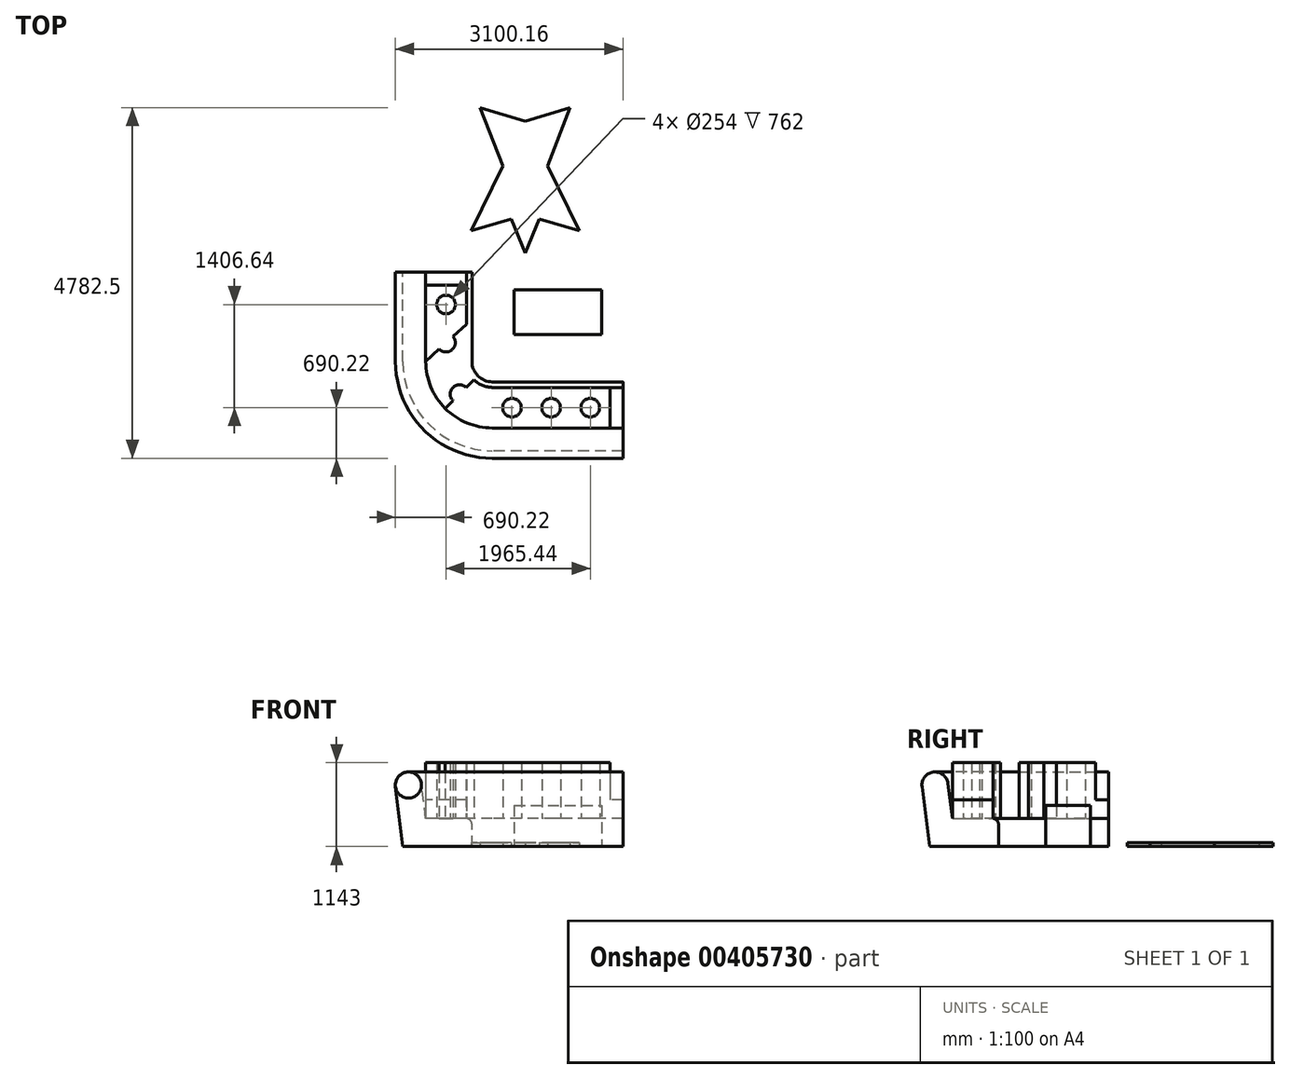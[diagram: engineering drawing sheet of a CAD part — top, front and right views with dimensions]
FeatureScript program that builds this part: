
annotation { "Feature Type Name" : "Feature", "Feature Type Description" : "" }
export const myFeature = defineFeature(function(context is Context, id is Id, definition is map)
    precondition{}
    {
        {
            var Q0;
            Q0=qCreatedBy(makeId("Right.planeOp"),FACE);
            var sketch = newSketch(context, id + "F0", { "sketchPlane" : qUnion([Q0])});
            skLineSegment(sketch, "E0", {"start": v(-101.6, 816.24) * mm, "end": v(0, 0) * mm});
            skLineSegment(sketch, "E1", {"start": v(0, 0) * mm, "end": v(939.8, 0) * mm});
            skLineSegment(sketch, "E2", {"start": v(939.8, 0) * mm, "end": v(939.8, 304.8) * mm});
            skLineSegment(sketch, "E3", {"start": v(863.6, 381) * mm, "end": v(310.92, 381) * mm});
            skLineSegment(sketch, "E4", {"start": v(310.92, 381) * mm, "end": v(251.28, 860.16) * mm});
            skLineSegment(sketch, "E5", {"start": v(251.28, 860.16) * mm, "end": v(-101.6, 816.24) * mm});
            skArc(sketch, "E6", {"start": v(251.28, 860.16) * mm, "mid": v(52.88, 1014.64) * mm, "end": v(-101.6, 816.24) * mm});
            skPoint(sketch, "E7.visualSharp", {"position": v(939.8, 381) * mm});
            skArc(sketch, "E7.filletArc", {"start": v(939.8, 304.8) * mm, "mid": v(917.48, 358.68) * mm, "end": v(863.6, 381) * mm});
            skSolve(sketch);
        }
        {
            var Q0;
            Q0=qCreatedBy(makeId("Top.planeOp"),FACE);
            var sketch = newSketch(context, id + "F1", { "sketchPlane" : qUnion([Q0])});
            skLineSegment(sketch, "E8", {"start": v(0, 0) * mm, "end": v(-1778, 0) * mm});
            skLineSegment(sketch, "E9", {"start": v(-2997.2, 1219.2) * mm, "end": v(-2997.2, 2438.4) * mm});
            skArc(sketch, "E10", {"start": v(-2997.2, 1219.2) * mm, "mid": v(-2640.1, 357.1) * mm, "end": v(-1778, 0) * mm});
            skSolve(sketch);
        }
        {
            var Q0;
            Q0=makeQuery(id+"F0.imprint","IMPRINT",FACE,{"disambiguationData":[TD([[makeQuery(id+"F0.imprint","IMPRINT",EDGE,{"derivedFrom":sQuery(id+"F0.wireOp",EDGE,"E0")}),1.0]])]});
            var Q1;
            Q1=makeQuery(id+"F0.imprint","IMPRINT",FACE,{"disambiguationData":[TD([[makeQuery(id+"F0.imprint","IMPRINT",EDGE,{"derivedFrom":sQuery(id+"F0.wireOp",EDGE,"E5")}),-1.0]])]});
            var Q2;
            Q2=sQuery(id+"F1.wireOp",EDGE,"E8");
            var Q3;
            Q3=sQuery(id+"F1.wireOp",EDGE,"E10");
            var Q4;
            Q4=sQuery(id+"F1.wireOp",EDGE,"E9");
            sweep(context, id + "F2", {"profiles" : qUnion([Q0, Q1]), "path" : qUnion([Q2, Q3, Q4])});
        }
        {
            var Q0;
            Q0=makeQuery(id+"F2.opSweep","SWEPT_FACE",FACE,{"disambiguationData":[OSD([sQuery(id+"F0.wireOp",EDGE,"E3"),sQuery(id+"F1.wireOp",EDGE,"E8")])]});
            var sketch = newSketch(context, id + "F3", { "sketchPlane" : qUnion([Q0])});
            skLineSegment(sketch, "E11.0", {"start": v(0, 863.6) * mm, "end": v(-1778, 863.6) * mm});
            skArc(sketch, "E11.1", {"start": v(-1778, 863.6) * mm, "mid": v(-2029.45, 967.75) * mm, "end": v(-2133.6, 1219.2) * mm});
            skLineSegment(sketch, "E11.2", {"start": v(-2133.6, 1219.2) * mm, "end": v(-2133.6, 2438.4) * mm});
            skLineSegment(sketch, "E11.3", {"start": v(-2686.28, 2438.4) * mm, "end": v(-2133.6, 2438.4) * mm});
            skLineSegment(sketch, "E11.4", {"start": v(-2686.28, 1219.2) * mm, "end": v(-2686.28, 2438.4) * mm});
            skArc(sketch, "E11.5", {"start": v(-1778, 310.92) * mm, "mid": v(-2420.25, 576.95) * mm, "end": v(-2686.28, 1219.2) * mm});
            skLineSegment(sketch, "E11.6", {"start": v(0, 310.92) * mm, "end": v(-1778, 310.92) * mm});
            skLineSegment(sketch, "E11.7", {"start": v(0, 310.92) * mm, "end": v(0, 863.6) * mm});
            skLineSegment(sketch, "E12", {"start": v(-177.8, 863.6) * mm, "end": v(-177.8, 310.92) * mm});
            skLineSegment(sketch, "E13", {"start": v(-2686.28, 2260.6) * mm, "end": v(-2133.6, 2260.6) * mm});
            skLineSegment(sketch, "E14", {"start": v(-1778, 310.92) * mm, "end": v(-1244.6, 863.6) * mm});
            skLineSegment(sketch, "E15", {"start": v(-1244.6, 863.6) * mm, "end": v(-711.2, 310.92) * mm});
            skLineSegment(sketch, "E16", {"start": v(-711.2, 310.92) * mm, "end": v(-177.8, 863.6) * mm});
            skLineSegment(sketch, "E17", {"start": v(-2686.28, 2260.6) * mm, "end": v(-2133.6, 1727.2) * mm});
            skLineSegment(sketch, "E18", {"start": v(-2133.6, 1727.2) * mm, "end": v(-2686.28, 1219.2) * mm});
            skPoint(sketch, "E19", {"position": v(-2409.94, 1993.9) * mm});
            skPoint(sketch, "E20", {"position": v(-2409.94, 1473.2) * mm});
            skPoint(sketch, "E21", {"position": v(-1511.3, 587.26) * mm});
            skPoint(sketch, "E22", {"position": v(-977.9, 587.26) * mm});
            skPoint(sketch, "E23", {"position": v(-444.5, 587.26) * mm});
            skLineSegment(sketch, "E24", {"start": v(-2029.45, 967.75) * mm, "end": v(-2420.25, 576.95) * mm});
            skPoint(sketch, "E25", {"position": v(-2224.85, 772.35) * mm});
            skCircle(sketch, "E26", {"center": v(-2409.94, 1473.2) * mm, "radius": 127 * mm});
            skCircle(sketch, "E27", {"center": v(-1511.3, 587.26) * mm, "radius": 127 * mm});
            skCircle(sketch, "E28", {"center": v(-977.9, 587.26) * mm, "radius": 127 * mm});
            skCircle(sketch, "E29", {"center": v(-444.5, 587.26) * mm, "radius": 127 * mm});
            skCircle(sketch, "E30", {"center": v(-2224.85, 772.35) * mm, "radius": 127 * mm});
            skCircle(sketch, "E31", {"center": v(-2409.94, 1993.9) * mm, "radius": 127 * mm});
            skSolve(sketch);
        }
        {
            var Q0;
            {var subQ0=sQuery(id+"F3.wireOp",EDGE,"E11.3");Q0=makeQuery(id+"F3.imprint","IMPRINT",FACE,{"disambiguationData":[TD([[makeQuery(id+"F3.imprint","IMPRINT",EDGE,{"derivedFrom":subQ0}),-1.0]])]});}
            var Q1;
            {var subQ0=sQuery(id+"F3.wireOp",EDGE,"E11.7");Q1=makeQuery(id+"F3.imprint","IMPRINT",FACE,{"disambiguationData":[TD([[makeQuery(id+"F3.imprint","IMPRINT",EDGE,{"derivedFrom":subQ0}),1.0]])]});}
            extrude(context, id + "F4", {"entities" : qUnion([Q0, Q1]), "operationType" : NewBodyOperationType.ADD, "depth" : 254 * mm, "offsetDistance" : 25.4 * mm});
        }
        {
            var Q0;
            {var subQ0=sQuery(id+"F3.wireOp",EDGE,"E29");var subQ1=sQuery(id+"F3.wireOp",EDGE,"E16");var subQ2=makeQuery(id+"F3.imprint","INTERSECT",VERTEX,{"disambiguationData":[OD(0.0)],"derivedFrom":[subQ1,subQ0]});Q0=makeQuery(id+"F3.imprint","IMPRINT",FACE,{"disambiguationData":[TD([[makeQuery(id+"F3.imprint","IMPRINT",EDGE,{"disambiguationData":[TD([[subQ2,-1.0]])],"derivedFrom":subQ1}),-1.0]])]});}
            var Q1;
            {var subQ0=sQuery(id+"F3.wireOp",EDGE,"E29");var subQ1=sQuery(id+"F3.wireOp",EDGE,"E16");var subQ2=makeQuery(id+"F3.imprint","INTERSECT",VERTEX,{"disambiguationData":[OD(0.0)],"derivedFrom":[subQ1,subQ0]});Q1=makeQuery(id+"F3.imprint","IMPRINT",FACE,{"disambiguationData":[TD([[makeQuery(id+"F3.imprint","IMPRINT",EDGE,{"disambiguationData":[TD([[subQ2,-1.0]])],"derivedFrom":subQ1}),1.0]])]});}
            var Q2;
            {var subQ0=sQuery(id+"F3.wireOp",EDGE,"E28");var subQ1=sQuery(id+"F3.wireOp",EDGE,"E15");var subQ2=makeQuery(id+"F3.imprint","INTERSECT",VERTEX,{"disambiguationData":[OD(0.0)],"derivedFrom":[subQ1,subQ0]});Q2=makeQuery(id+"F3.imprint","IMPRINT",FACE,{"disambiguationData":[TD([[makeQuery(id+"F3.imprint","IMPRINT",EDGE,{"disambiguationData":[TD([[subQ2,-1.0]])],"derivedFrom":subQ1}),1.0]])]});}
            var Q3;
            {var subQ0=sQuery(id+"F3.wireOp",EDGE,"E28");var subQ1=sQuery(id+"F3.wireOp",EDGE,"E15");var subQ2=makeQuery(id+"F3.imprint","INTERSECT",VERTEX,{"disambiguationData":[OD(0.0)],"derivedFrom":[subQ1,subQ0]});Q3=makeQuery(id+"F3.imprint","IMPRINT",FACE,{"disambiguationData":[TD([[makeQuery(id+"F3.imprint","IMPRINT",EDGE,{"disambiguationData":[TD([[subQ2,-1.0]])],"derivedFrom":subQ1}),-1.0]])]});}
            var Q4;
            {var subQ0=sQuery(id+"F3.wireOp",EDGE,"E27");var subQ1=sQuery(id+"F3.wireOp",EDGE,"E14");var subQ2=makeQuery(id+"F3.imprint","INTERSECT",VERTEX,{"disambiguationData":[OD(0.0)],"derivedFrom":[subQ1,subQ0]});Q4=makeQuery(id+"F3.imprint","IMPRINT",FACE,{"disambiguationData":[TD([[makeQuery(id+"F3.imprint","IMPRINT",EDGE,{"disambiguationData":[TD([[subQ2,-1.0]])],"derivedFrom":subQ1}),1.0]])]});}
            var Q5;
            {var subQ0=sQuery(id+"F3.wireOp",EDGE,"E27");var subQ1=sQuery(id+"F3.wireOp",EDGE,"E14");var subQ2=makeQuery(id+"F3.imprint","INTERSECT",VERTEX,{"disambiguationData":[OD(0.0)],"derivedFrom":[subQ1,subQ0]});Q5=makeQuery(id+"F3.imprint","IMPRINT",FACE,{"disambiguationData":[TD([[makeQuery(id+"F3.imprint","IMPRINT",EDGE,{"disambiguationData":[TD([[subQ2,-1.0]])],"derivedFrom":subQ1}),-1.0]])]});}
            var Q6;
            {var subQ0=sQuery(id+"F3.wireOp",EDGE,"E30");var subQ1=sQuery(id+"F3.wireOp",EDGE,"E24");var subQ2=makeQuery(id+"F3.imprint","INTERSECT",VERTEX,{"disambiguationData":[OD(0.0)],"derivedFrom":[subQ1,subQ0]});Q6=makeQuery(id+"F3.imprint","IMPRINT",FACE,{"disambiguationData":[TD([[makeQuery(id+"F3.imprint","IMPRINT",EDGE,{"disambiguationData":[TD([[subQ2,-1.0]])],"derivedFrom":subQ1}),-1.0]])]});}
            var Q7;
            {var subQ0=sQuery(id+"F3.wireOp",EDGE,"E30");var subQ1=sQuery(id+"F3.wireOp",EDGE,"E24");var subQ2=makeQuery(id+"F3.imprint","INTERSECT",VERTEX,{"disambiguationData":[OD(0.0)],"derivedFrom":[subQ1,subQ0]});Q7=makeQuery(id+"F3.imprint","IMPRINT",FACE,{"disambiguationData":[TD([[makeQuery(id+"F3.imprint","IMPRINT",EDGE,{"disambiguationData":[TD([[subQ2,-1.0]])],"derivedFrom":subQ1}),1.0]])]});}
            var Q8;
            {var subQ0=sQuery(id+"F3.wireOp",EDGE,"E26");var subQ1=sQuery(id+"F3.wireOp",EDGE,"E18");var subQ2=makeQuery(id+"F3.imprint","INTERSECT",VERTEX,{"disambiguationData":[OD(0.0)],"derivedFrom":[subQ1,subQ0]});Q8=makeQuery(id+"F3.imprint","IMPRINT",FACE,{"disambiguationData":[TD([[makeQuery(id+"F3.imprint","IMPRINT",EDGE,{"disambiguationData":[TD([[subQ2,-1.0]])],"derivedFrom":subQ1}),-1.0]])]});}
            var Q9;
            {var subQ0=sQuery(id+"F3.wireOp",EDGE,"E26");var subQ1=sQuery(id+"F3.wireOp",EDGE,"E18");var subQ2=makeQuery(id+"F3.imprint","INTERSECT",VERTEX,{"disambiguationData":[OD(0.0)],"derivedFrom":[subQ1,subQ0]});Q9=makeQuery(id+"F3.imprint","IMPRINT",FACE,{"disambiguationData":[TD([[makeQuery(id+"F3.imprint","IMPRINT",EDGE,{"disambiguationData":[TD([[subQ2,-1.0]])],"derivedFrom":subQ1}),1.0]])]});}
            var Q10;
            {var subQ0=sQuery(id+"F3.wireOp",EDGE,"E31");var subQ1=sQuery(id+"F3.wireOp",EDGE,"E17");var subQ2=makeQuery(id+"F3.imprint","INTERSECT",VERTEX,{"disambiguationData":[OD(0.0)],"derivedFrom":[subQ1,subQ0]});Q10=makeQuery(id+"F3.imprint","IMPRINT",FACE,{"disambiguationData":[TD([[makeQuery(id+"F3.imprint","IMPRINT",EDGE,{"disambiguationData":[TD([[subQ2,-1.0]])],"derivedFrom":subQ1}),-1.0]])]});}
            var Q11;
            {var subQ0=sQuery(id+"F3.wireOp",EDGE,"E31");var subQ1=sQuery(id+"F3.wireOp",EDGE,"E17");var subQ2=makeQuery(id+"F3.imprint","INTERSECT",VERTEX,{"disambiguationData":[OD(0.0)],"derivedFrom":[subQ1,subQ0]});Q11=makeQuery(id+"F3.imprint","IMPRINT",FACE,{"disambiguationData":[TD([[makeQuery(id+"F3.imprint","IMPRINT",EDGE,{"disambiguationData":[TD([[subQ2,-1.0]])],"derivedFrom":subQ1}),1.0]])]});}
            extrude(context, id + "F5", {"entities" : qUnion([Q0, Q1, Q2, Q3, Q4, Q5, Q6, Q7, Q8, Q9, Q10, Q11]), "operationType" : NewBodyOperationType.ADD, "depth" : 762 * mm, "offsetDistance" : 25.4 * mm});
        }
        {
            var Q0;
            Q0=qCreatedBy(makeId("Top.planeOp"),FACE);
            var sketch = newSketch(context, id + "F6", { "sketchPlane" : qUnion([Q0])});
            skLineSegment(sketch, "E32.bottom", {"start": v(-1481.62, 2191.92) * mm, "end": v(-287.82, 2191.92) * mm});
            skLineSegment(sketch, "E32.top", {"start": v(-1481.62, 1582.32) * mm, "end": v(-287.82, 1582.32) * mm});
            skLineSegment(sketch, "E32.left", {"start": v(-1481.62, 2191.92) * mm, "end": v(-1481.62, 1582.32) * mm});
            skLineSegment(sketch, "E32.right", {"start": v(-287.82, 2191.92) * mm, "end": v(-287.82, 1582.32) * mm});
            skLineSegment(sketch, "E33", {"start": v(-1333.52, 2698.34) * mm, "end": v(-1524.02, 3160.9) * mm});
            skLineSegment(sketch, "E34", {"start": v(-1524.02, 3160.9) * mm, "end": v(-2070.12, 3003.14) * mm});
            skLineSegment(sketch, "E35", {"start": v(-2070.12, 3003.14) * mm, "end": v(-1638.32, 3883.35) * mm});
            skLineSegment(sketch, "E36", {"start": v(-1638.32, 3883.35) * mm, "end": v(-1943.12, 4679.54) * mm});
            skLineSegment(sketch, "E37", {"start": v(-1943.12, 4679.54) * mm, "end": v(-1333.52, 4492.95) * mm});
            skLineSegment(sketch, "E38", {"start": v(-1333.52, 2698.34) * mm, "end": v(-1333.52, 4492.95) * mm, "construction": true});
            skLineSegment(sketch, "E39.MirrorCS", {"start": v(-1333.52, 2698.34) * mm, "end": v(-1143.02, 3160.9) * mm});
            skLineSegment(sketch, "E40.MirrorCS", {"start": v(-1143.02, 3160.9) * mm, "end": v(-596.92, 3003.14) * mm});
            skLineSegment(sketch, "E41.MirrorCS", {"start": v(-596.92, 3003.14) * mm, "end": v(-1028.72, 3883.35) * mm});
            skLineSegment(sketch, "E42.MirrorCS", {"start": v(-1028.72, 3883.35) * mm, "end": v(-723.92, 4679.54) * mm});
            skLineSegment(sketch, "E43.MirrorCS", {"start": v(-723.92, 4679.54) * mm, "end": v(-1333.52, 4492.95) * mm});
            skSolve(sketch);
        }
        {
            var Q0;
            Q0=makeQuery(id+"F6.imprint","IMPRINT",FACE,{"disambiguationData":[TD([[makeQuery(id+"F6.imprint","IMPRINT",EDGE,{"derivedFrom":sQuery(id+"F6.wireOp",EDGE,"E32.bottom")}),-1.0]])]});
            extrude(context, id + "F7", {"entities" : qUnion([Q0]), "depth" : 558.8 * mm, "offsetDistance" : 25.4 * mm});
        }
        {
            var Q0;
            Q0=makeQuery(id+"F6.imprint","IMPRINT",FACE,{"disambiguationData":[TD([[makeQuery(id+"F6.imprint","IMPRINT",EDGE,{"derivedFrom":sQuery(id+"F6.wireOp",EDGE,"E33")}),-1.0]])]});
            extrude(context, id + "F8", {"entities" : qUnion([Q0]), "depth" : 50.8 * mm, "offsetDistance" : 25.4 * mm});
        }
    });
